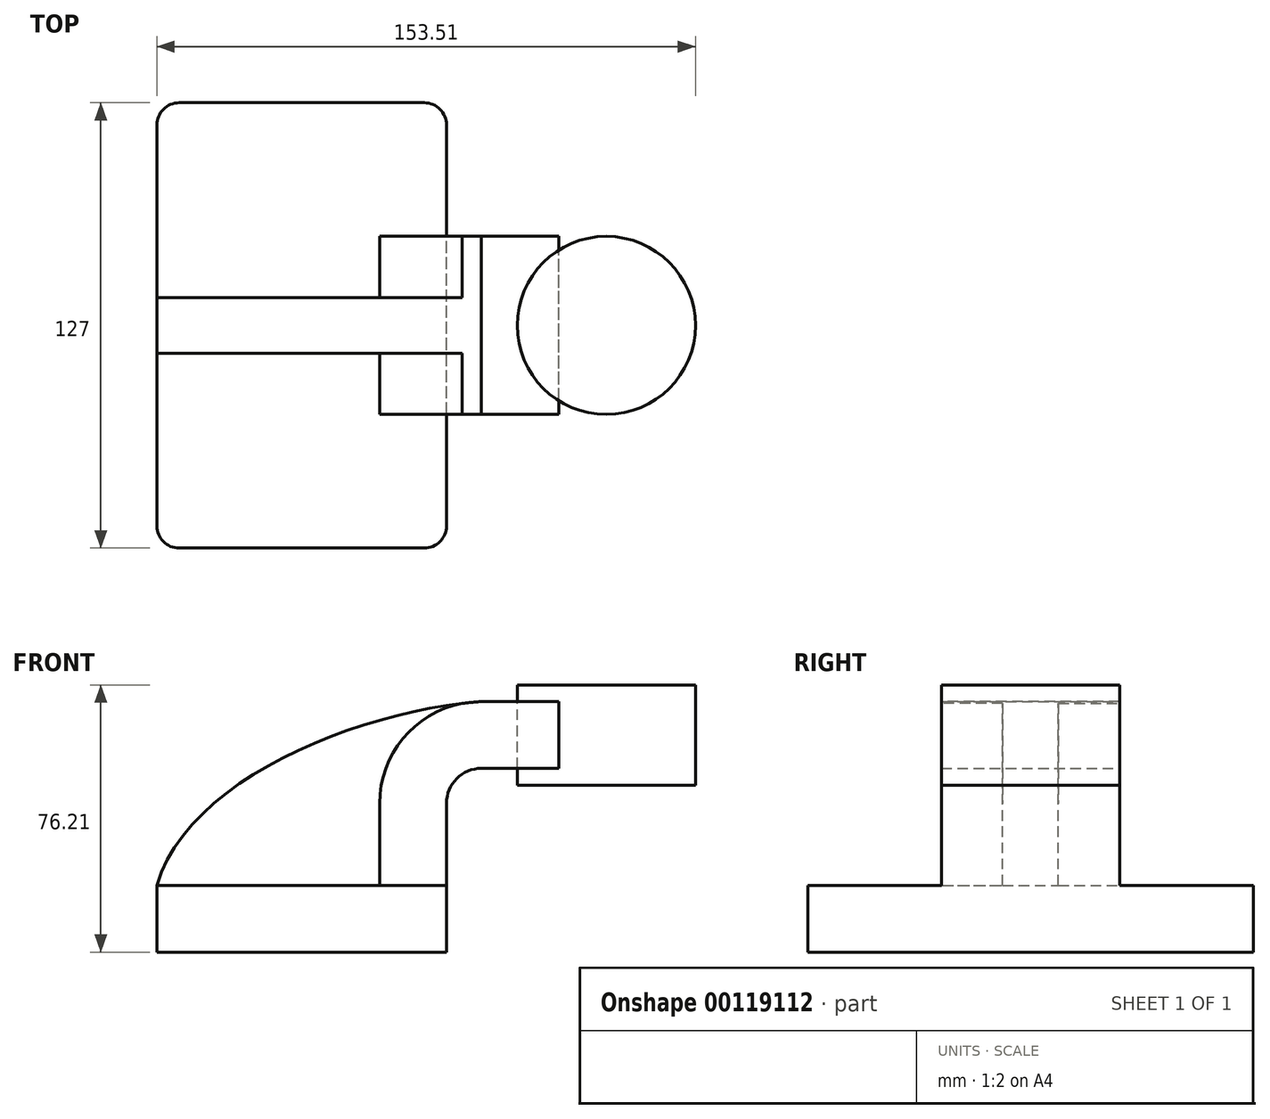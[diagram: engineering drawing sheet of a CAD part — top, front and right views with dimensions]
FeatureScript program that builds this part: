
annotation { "Feature Type Name" : "Feature", "Feature Type Description" : "" }
export const myFeature = defineFeature(function(context is Context, id is Id, definition is map)
    precondition{}
    {
        {
            var Q0;
            Q0=qCreatedBy(makeId("Front.planeOp"),FACE);
            var sketch = newSketch(context, id + "F0", { "sketchPlane" : qUnion([Q0])});
            skLineSegment(sketch, "E0.bottom", {"start": v(-41.27, -9.53) * mm, "end": v(41.28, -9.53) * mm});
            skLineSegment(sketch, "E0.top", {"start": v(-41.28, 9.53) * mm, "end": v(41.28, 9.53) * mm});
            skLineSegment(sketch, "E0.left", {"start": v(-41.28, -9.53) * mm, "end": v(-41.28, 9.53) * mm});
            skLineSegment(sketch, "E0.right", {"start": v(41.28, -9.53) * mm, "end": v(41.28, 9.53) * mm});
            skPoint(sketch, "E0.middle", {"position": v(0, 0) * mm});
            skLineSegment(sketch, "E1.bottom", {"start": v(61.43, 38.1) * mm, "end": v(112.23, 38.1) * mm});
            skLineSegment(sketch, "E1.top", {"start": v(61.43, 66.68) * mm, "end": v(112.23, 66.68) * mm});
            skLineSegment(sketch, "E1.left", {"start": v(61.43, 38.1) * mm, "end": v(61.43, 66.68) * mm});
            skLineSegment(sketch, "E1.right", {"start": v(112.23, 38.1) * mm, "end": v(112.23, 66.68) * mm});
            skPoint(sketch, "E1.middle", {"position": v(86.83, 52.39) * mm});
            skLineSegment(sketch, "E2", {"start": v(41.28, 9.53) * mm, "end": v(41.28, 32.9) * mm});
            skArc(sketch, "E3", {"start": v(41.27, 32.9) * mm, "mid": v(44.2, 39.95) * mm, "end": v(51.25, 42.88) * mm});
            skLineSegment(sketch, "E4", {"start": v(51.25, 42.88) * mm, "end": v(73.24, 42.88) * mm});
            skLineSegment(sketch, "E5.0", {"start": v(51.25, 61.93) * mm, "end": v(73.24, 61.93) * mm});
            skArc(sketch, "E5.1", {"start": v(22.22, 32.9) * mm, "mid": v(30.73, 53.42) * mm, "end": v(51.25, 61.93) * mm});
            skLineSegment(sketch, "E5.2", {"start": v(22.22, 9.53) * mm, "end": v(22.22, 32.9) * mm});
            skLineSegment(sketch, "E6", {"start": v(73.24, 61.93) * mm, "end": v(73.24, 42.88) * mm});
            skFitSpline(sketch, "E7", {"points": [v(-41.27, 9.52) * mm, v(51.25, 61.93) * mm], "startDerivative": vector(26.46, 91) * mm, "endDerivative": vector(104.97, 7.75) * mm});
            skLineSegment(sketch, "E8", {"start": v(86.83, 66.68) * mm, "end": v(86.83, 38.1) * mm});
            skSolve(sketch);
        }
        {
            var Q0;
            Q0=makeQuery(id+"F0.imprint","IMPRINT",FACE,{"disambiguationData":[TD([[makeQuery(id+"F0.imprint","IMPRINT",EDGE,{"derivedFrom":sQuery(id+"F0.wireOp",EDGE,"E0.bottom")}),1.0]])]});
            extrude(context, id + "F1", {"entities" : qUnion([Q0]), "endBound" : BoundingType.SYMMETRIC, "depth" : 127 * mm});
        }
        {
            var Q0;
            {var subQ1=sQuery(id+"F0.wireOp",EDGE,"E2");Q0=makeQuery(id+"F0.imprint","IMPRINT",FACE,{"disambiguationData":[TD([[makeQuery(id+"F0.imprint","IMPRINT",EDGE,{"derivedFrom":subQ1}),1.0]])]});}
            var Q1;
            {var subQ5=sQuery(id+"F0.wireOp",EDGE,"E6");Q1=makeQuery(id+"F0.imprint","IMPRINT",FACE,{"disambiguationData":[TD([[makeQuery(id+"F0.imprint","IMPRINT",EDGE,{"derivedFrom":subQ5}),-1.0]])]});}
            extrude(context, id + "F2", {"entities" : qUnion([Q0, Q1]), "operationType" : NewBodyOperationType.ADD, "endBound" : BoundingType.SYMMETRIC, "depth" : 50.8 * mm});
        }
        {
            var Q0;
            {var subQ3=sQuery(id+"F0.wireOp",EDGE,"E5.2");Q0=makeQuery(id+"F0.imprint","IMPRINT",FACE,{"disambiguationData":[TD([[makeQuery(id+"F0.imprint","IMPRINT",EDGE,{"derivedFrom":subQ3}),1.0]])]});}
            extrude(context, id + "F3", {"entities" : qUnion([Q0]), "operationType" : NewBodyOperationType.ADD, "endBound" : BoundingType.SYMMETRIC, "depth" : 15.88 * mm});
        }
        {
            var Q0;
            {var subQ0=sQuery(id+"F0.wireOp",EDGE,"E1.right");Q0=makeQuery(id+"F0.imprint","IMPRINT",FACE,{"disambiguationData":[TD([[makeQuery(id+"F0.imprint","IMPRINT",EDGE,{"derivedFrom":subQ0}),1.0]])]});}
            var Q1;
            Q1=sQuery(id+"F0.wireOp",EDGE,"E8");
            revolve(context, id + "F4", {"entities" : qUnion([Q0]), "axis" : qUnion([Q1]), "revolveType" : RevolveType.FULL});
        }
        {
            var Q0;
            Q0=makeQuery(id+"F1.opExtrude","CAP_EDGE",EDGE,{"disambiguationData":[OSD([sQuery(id+"F0.wireOp",EDGE,"E0.left")])],"isStart":false});
            var Q1;
            Q1=makeQuery(id+"F1.opExtrude","CAP_EDGE",EDGE,{"disambiguationData":[OSD([sQuery(id+"F0.wireOp",EDGE,"E0.left")])],"isStart":true});
            var Q2;
            Q2=makeQuery(id+"F1.opExtrude","CAP_EDGE",EDGE,{"disambiguationData":[OSD([sQuery(id+"F0.wireOp",EDGE,"E0.right")])],"isStart":false});
            var Q3;
            Q3=makeQuery(id+"F1.opExtrude","CAP_EDGE",EDGE,{"disambiguationData":[OSD([sQuery(id+"F0.wireOp",EDGE,"E0.right")])],"isStart":true});
            fillet(context, id + "F5", {"entities" : qUnion([Q0, Q1, Q2, Q3]), "radius" : 6.35 * mm, "tangentPropagation" : true, "allowEdgeOverflow" : false});
        }
    });
